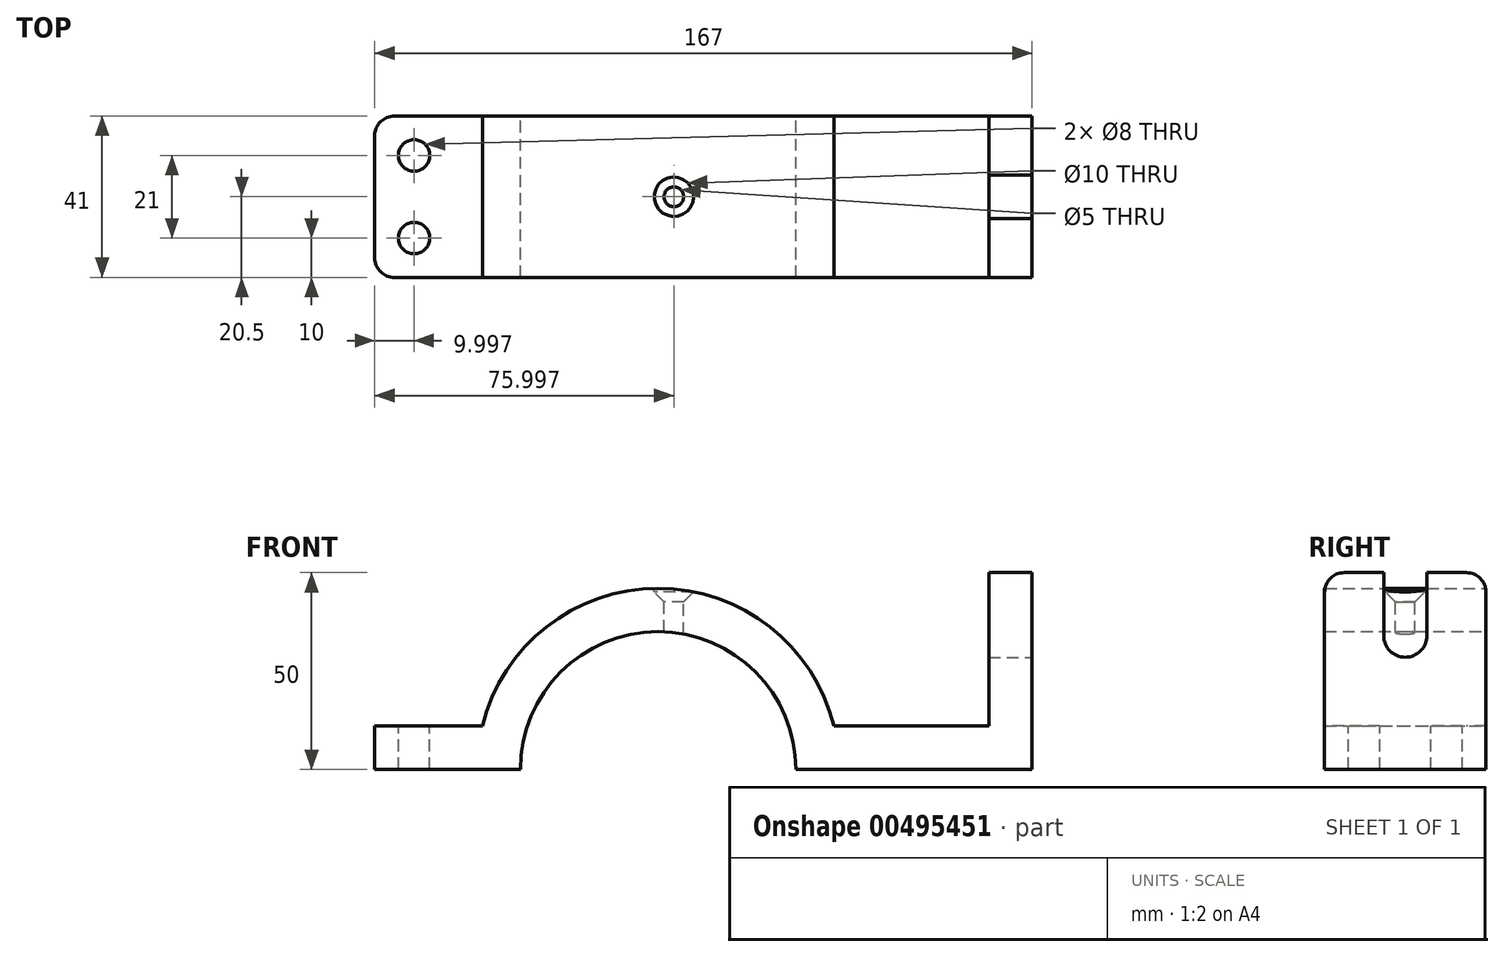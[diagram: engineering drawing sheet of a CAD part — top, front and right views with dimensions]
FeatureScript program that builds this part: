
annotation { "Feature Type Name" : "Feature", "Feature Type Description" : "" }
export const myFeature = defineFeature(function(context is Context, id is Id, definition is map)
    precondition{}
    {
        {
            var Q0;
            Q0=qCreatedBy(makeId("Front.planeOp"),FACE);
            var sketch = newSketch(context, id + "F0", { "sketchPlane" : qUnion([Q0])});
            skLineSegment(sketch, "E0.bottom", {"start": v(-97.24, 11) * mm, "end": v(-71.24, 11) * mm});
            skLineSegment(sketch, "E0.top", {"start": v(-97.24, 0) * mm, "end": v(-71.24, 0) * mm});
            skLineSegment(sketch, "E0.left", {"start": v(-97.24, 11) * mm, "end": v(-97.24, 0) * mm});
            skLineSegment(sketch, "E0.right", {"start": v(-71.24, 11) * mm, "end": v(-71.24, 0) * mm});
            skLineSegment(sketch, "E1.bottom", {"start": v(20.76, 11) * mm, "end": v(58.76, 11) * mm});
            skLineSegment(sketch, "E1.top", {"start": v(20.76, 0) * mm, "end": v(58.76, 0) * mm});
            skLineSegment(sketch, "E1.left", {"start": v(20.76, 11) * mm, "end": v(20.76, 0) * mm});
            skLineSegment(sketch, "E1.right", {"start": v(58.76, 11) * mm, "end": v(58.76, 0) * mm});
            skLineSegment(sketch, "E2.bottom", {"start": v(69.76, 0) * mm, "end": v(58.76, 0) * mm});
            skLineSegment(sketch, "E2.top", {"start": v(69.76, 50) * mm, "end": v(58.76, 50) * mm});
            skLineSegment(sketch, "E2.left", {"start": v(58.76, 0) * mm, "end": v(58.76, 50) * mm});
            skLineSegment(sketch, "E2.right", {"start": v(69.76, 0) * mm, "end": v(69.76, 50) * mm});
            skLineSegment(sketch, "E3.bottom", {"start": v(-71.24, 11) * mm, "end": v(-60.24, 11) * mm});
            skLineSegment(sketch, "E3.top", {"start": v(-71.24, 0) * mm, "end": v(-60.24, 0) * mm});
            skLineSegment(sketch, "E4.bottom", {"start": v(20.76, 11) * mm, "end": v(9.76, 11) * mm});
            skLineSegment(sketch, "E4.top", {"start": v(20.76, 0) * mm, "end": v(9.76, 0) * mm});
            skLineSegment(sketch, "E5", {"start": v(-60.24, 0) * mm, "end": v(9.76, 0) * mm});
            skPoint(sketch, "E6", {"position": v(-25.24, 0) * mm});
            skCircle(sketch, "E7", {"center": v(-25.24, 0) * mm, "radius": 35 * mm});
            skCircle(sketch, "E8", {"center": v(-25.24, 0) * mm, "radius": 46 * mm});
            skSolve(sketch);
        }
        {
            var Q0;
            Q0=makeQuery(id+"F0.imprint","IMPRINT",FACE,{"disambiguationData":[TD([[makeQuery(id+"F0.imprint","IMPRINT",EDGE,{"derivedFrom":sQuery(id+"F0.wireOp",EDGE,"E0.bottom")}),-1.0]])]});
            var Q1;
            Q1=makeQuery(id+"F0.imprint","IMPRINT",FACE,{"disambiguationData":[TD([[makeQuery(id+"F0.imprint","IMPRINT",EDGE,{"derivedFrom":sQuery(id+"F0.wireOp",EDGE,"E3.bottom")}),-1.0]])]});
            var Q2;
            Q2=makeQuery(id+"F0.imprint","IMPRINT",FACE,{"disambiguationData":[TD([[makeQuery(id+"F0.imprint","IMPRINT",EDGE,{"derivedFrom":sQuery(id+"F0.wireOp",EDGE,"Smr86giT-9eCB-g6Qo-ZvQA-M9UJpJssD94v")}),1.0]])]});
            var Q3;
            Q3=makeQuery(id+"F0.imprint","IMPRINT",FACE,{"disambiguationData":[TD([[makeQuery(id+"F0.imprint","IMPRINT",EDGE,{"derivedFrom":sQuery(id+"F0.wireOp",EDGE,"E4.bottom")}),1.0]])]});
            var Q4;
            {var subQ0=sQuery(id+"F0.wireOp",EDGE,"E1.bottom");Q4=makeQuery(id+"F0.imprint","IMPRINT",FACE,{"disambiguationData":[TD([[makeQuery(id+"F0.imprint","IMPRINT",EDGE,{"derivedFrom":subQ0}),-1.0]])]});}
            var Q5;
            {var subQ3=sQuery(id+"F0.wireOp",EDGE,"E2.bottom");Q5=makeQuery(id+"F0.imprint","IMPRINT",FACE,{"disambiguationData":[TD([[makeQuery(id+"F0.imprint","IMPRINT",EDGE,{"derivedFrom":subQ3}),-1.0]])]});}
            var Q6;
            {var subQ2=sQuery(id+"F0.wireOp",EDGE,"E3.top");Q6=makeQuery(id+"F0.imprint","IMPRINT",FACE,{"disambiguationData":[TD([[makeQuery(id+"F0.imprint","IMPRINT",EDGE,{"derivedFrom":subQ2}),1.0]])]});}
            extrude(context, id + "F1", {"entities" : qUnion([Q0, Q1, Q2, Q3, Q4, Q5, Q6]), "endBound" : BoundingType.SYMMETRIC, "depth" : 41 * mm});
        }
        {
            var Q0;
            Q0=makeQuery(id+"F1.opExtrude","CAP_EDGE",EDGE,{"disambiguationData":[OSD([sQuery(id+"F0.wireOp",EDGE,"E0.left")])],"isStart":false});
            var Q1;
            Q1=makeQuery(id+"F1.opExtrude","CAP_EDGE",EDGE,{"disambiguationData":[OSD([sQuery(id+"F0.wireOp",EDGE,"E0.left")])],"isStart":true});
            fillet(context, id + "F2", {"entities" : qUnion([Q0, Q1]), "radius" : 5 * mm, "tangentPropagation" : true, "allowEdgeOverflow" : false});
        }
        {
            var Q0;
            Q0=makeQuery(id+"F1.opExtrude","CAP_EDGE",EDGE,{"disambiguationData":[OSD([sQuery(id+"F0.wireOp",EDGE,"E2.top")])],"isStart":false});
            var Q1;
            Q1=makeQuery(id+"F1.opExtrude","CAP_EDGE",EDGE,{"disambiguationData":[OSD([sQuery(id+"F0.wireOp",EDGE,"E2.top")])],"isStart":true});
            fillet(context, id + "F3", {"entities" : qUnion([Q0, Q1]), "radius" : 5 * mm, "tangentPropagation" : true, "allowEdgeOverflow" : false});
        }
        {
            var Q0;
            Q0=makeQuery(id+"F1.opExtrude","SWEPT_FACE",FACE,{"disambiguationData":[OSD([sQuery(id+"F0.wireOp",EDGE,"E0.bottom")])]});
            var sketch = newSketch(context, id + "F4", { "sketchPlane" : qUnion([Q0])});
            skCircle(sketch, "E9", {"center": v(-87.24, 10.5) * mm, "radius": 4 * mm});
            skCircle(sketch, "E10", {"center": v(-87.24, -10.5) * mm, "radius": 4 * mm});
            skSolve(sketch);
        }
        {
            var Q0;
            Q0=makeQuery(id+"F4.imprint","IMPRINT",FACE,{"disambiguationData":[TD([[makeQuery(id+"F4.imprint","IMPRINT",EDGE,{"derivedFrom":sQuery(id+"F4.wireOp",EDGE,"E9")}),1.0]])]});
            var Q1;
            Q1=makeQuery(id+"F4.imprint","IMPRINT",FACE,{"disambiguationData":[TD([[makeQuery(id+"F4.imprint","IMPRINT",EDGE,{"derivedFrom":sQuery(id+"F4.wireOp",EDGE,"E10")}),1.0]])]});
            var Q2;
            Q2=sQuery(id+"F4.wireOp",EDGE,"E9");
            var Q3;
            Q3=sQuery(id+"F4.wireOp",EDGE,"E10");
            extrude(context, id + "F5", {"entities" : qUnion([Q0, Q1]), "operationType" : NewBodyOperationType.REMOVE, "surfaceEntities" : qUnion([Q2, Q3]), "depth" : -12 * mm});
        }
        {
            var Q0;
            Q0=makeQuery(id+"F1.opExtrude","SWEPT_FACE",FACE,{"disambiguationData":[OSD([sQuery(id+"F0.wireOp",EDGE,"E2.right")])]});
            var sketch = newSketch(context, id + "F6", { "sketchPlane" : qUnion([Q0])});
            skLineSegment(sketch, "E11.bottom", {"start": v(-5.5, 50) * mm, "end": v(5.5, 50) * mm});
            skLineSegment(sketch, "E11.top", {"start": v(-5.5, 34) * mm, "end": v(5.5, 34) * mm});
            skLineSegment(sketch, "E11.left", {"start": v(-5.5, 50) * mm, "end": v(-5.5, 34) * mm});
            skLineSegment(sketch, "E11.right", {"start": v(5.5, 50) * mm, "end": v(5.5, 34) * mm});
            skCircle(sketch, "E12", {"center": v(0, 34) * mm, "radius": 5.5 * mm});
            skLineSegment(sketch, "E13.bottom", {"start": v(5.5, 34) * mm, "end": v(20.5, 34) * mm});
            skLineSegment(sketch, "E13.top", {"start": v(5.5, 45) * mm, "end": v(20.5, 45) * mm});
            skLineSegment(sketch, "E13.left", {"start": v(5.5, 34) * mm, "end": v(5.5, 45) * mm});
            skLineSegment(sketch, "E13.right", {"start": v(20.5, 34) * mm, "end": v(20.5, 45) * mm});
            skLineSegment(sketch, "E14.bottom", {"start": v(-5.5, 34) * mm, "end": v(-20.5, 34) * mm});
            skLineSegment(sketch, "E14.top", {"start": v(-5.5, 45) * mm, "end": v(-20.5, 45) * mm});
            skLineSegment(sketch, "E14.left", {"start": v(-5.5, 34) * mm, "end": v(-5.5, 45) * mm});
            skLineSegment(sketch, "E14.right", {"start": v(-20.5, 34) * mm, "end": v(-20.5, 45) * mm});
            skSolve(sketch);
        }
        {
            var Q0;
            Q0=makeQuery(id+"F6.imprint","IMPRINT",FACE,{"disambiguationData":[TD([[makeQuery(id+"F6.imprint","IMPRINT",EDGE,{"derivedFrom":sQuery(id+"F6.wireOp",EDGE,"E11.bottom")}),-1.0]])]});
            var Q1;
            {var subQ0=sQuery(id+"F6.wireOp",EDGE,"E11.top");Q1=makeQuery(id+"F6.imprint","IMPRINT",FACE,{"disambiguationData":[TD([[makeQuery(id+"F6.imprint","IMPRINT",EDGE,{"derivedFrom":subQ0}),1.0]])]});}
            var Q2;
            {var subQ0=sQuery(id+"F6.wireOp",EDGE,"E11.top");Q2=makeQuery(id+"F6.imprint","IMPRINT",FACE,{"disambiguationData":[TD([[makeQuery(id+"F6.imprint","IMPRINT",EDGE,{"derivedFrom":subQ0}),-1.0]])]});}
            extrude(context, id + "F7", {"entities" : qUnion([Q0, Q1, Q2]), "operationType" : NewBodyOperationType.REMOVE, "oppositeDirection" : true, "depth" : 25 * mm});
        }
        {
            var Q0;
            {var subQ0=sQuery(id+"F0.wireOp",EDGE,"E2.top");Q0=makeQuery(id+"F7.boolean.opBoolean","SPLIT",FACE,{"disambiguationData":[TD([makeQuery(id+"F3.opFillet","BLEND_FACE",FACE,{"disambiguationData":[OSD([subQ0]),TDD([makeQuery(id+"F1.opExtrude","CAP_EDGE",EDGE,{"disambiguationData":[OSD([subQ0])],"isStart":false})])]})])],"derivedFrom":makeQuery(id+"F1.opExtrude","SWEPT_FACE",FACE,{"disambiguationData":[OSD([subQ0])]})});}
            var sketch = newSketch(context, id + "F8", { "sketchPlane" : qUnion([Q0])});
            skPoint(sketch, "E15", {"position": v(-21.24, 0) * mm});
            skLineSegment(sketch, "E16", {"start": v(58.76, -5.5) * mm, "end": v(-21.24, 0) * mm});
            skLineSegment(sketch, "E17", {"start": v(-21.24, 0) * mm, "end": v(58.76, -5.5) * mm});
            skSolve(sketch);
        }
        {
            var Q0;
            Q0=sQuery(id+"F8.wireOp",VERTEX,"E15");
            var Q1;
            Q1=makeQuery(id+"F1.opExtrude","SWEPT_BODY",BODY,{"disambiguationData":[OSD([sQuery(id+"F0.wireOp",EDGE,"E0.bottom"),sQuery(id+"F0.wireOp",EDGE,"E0.top"),sQuery(id+"F0.wireOp",EDGE,"E0.left"),sQuery(id+"F0.wireOp",EDGE,"E1.bottom"),sQuery(id+"F0.wireOp",EDGE,"E1.top"),sQuery(id+"F0.wireOp",EDGE,"E2.bottom"),sQuery(id+"F0.wireOp",EDGE,"E2.top"),sQuery(id+"F0.wireOp",EDGE,"E2.left"),sQuery(id+"F0.wireOp",EDGE,"E2.right"),sQuery(id+"F0.wireOp",EDGE,"Smr86giT-9eCB-g6Qo-ZvQA-M9UJpJssD94v"),sQuery(id+"F0.wireOp",EDGE,"E3.top"),sQuery(id+"F0.wireOp",EDGE,"E3.right"),sQuery(id+"F0.wireOp",EDGE,"E4.top"),sQuery(id+"F0.wireOp",EDGE,"E4.right"),sQuery(id+"F0.wireOp",EDGE,"sHrFzfpQ-Ra8i-HdVC-d1aD-iQFfKQGGExt1")])]});
            hole(context, id + "F9", {"style" : HoleStyle.C_SINK, "endStyle" : HoleEndStyle.THROUGH, "holeDiameter" : 5 * mm, "cSinkDiameter" : 10 * mm, "cSinkAngle" : 90 * degree, "tappedDepth" : 12 * mm, "tapClearance" : 3, "locations" : qUnion([Q0]), "scope" : qUnion([Q1])});
        }
    });
